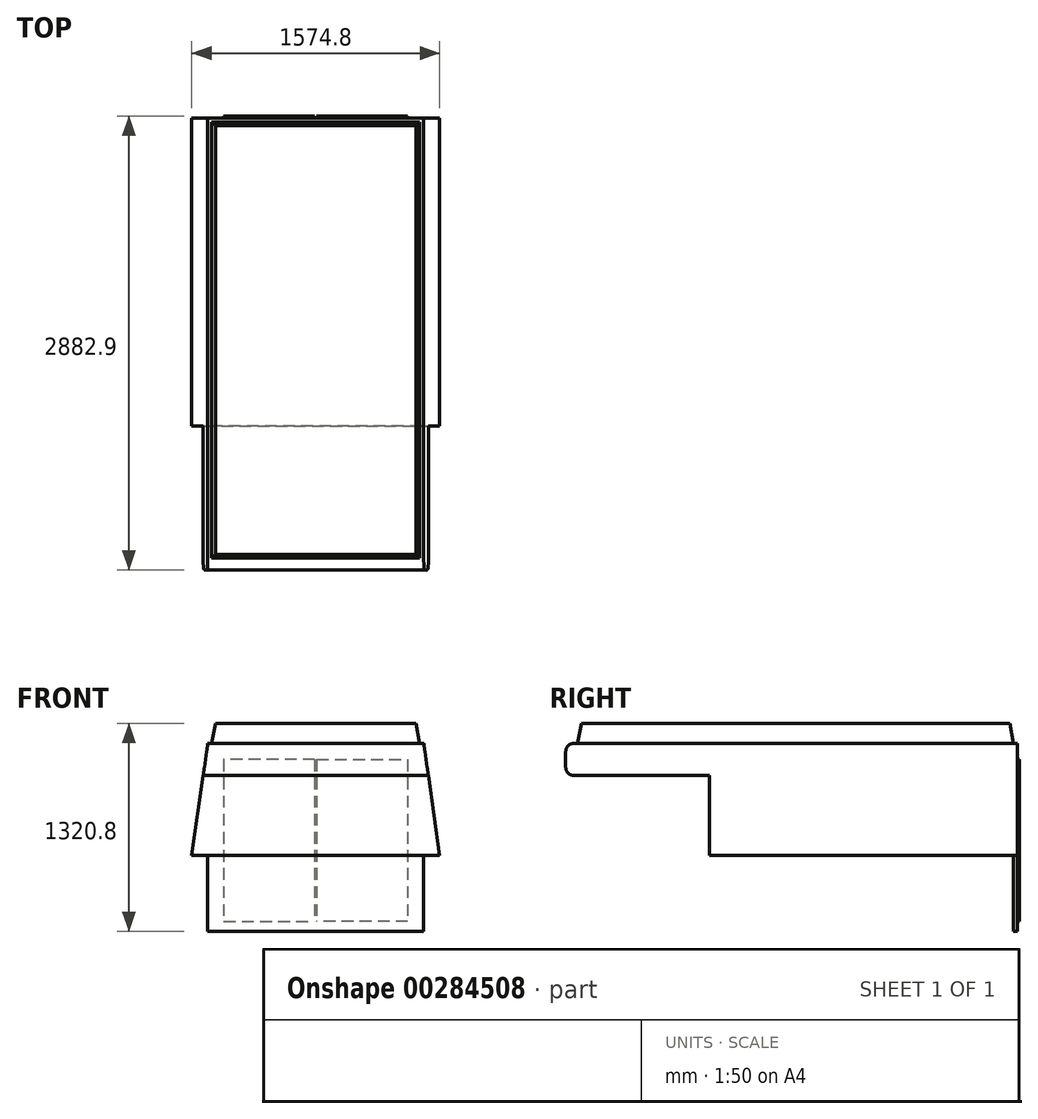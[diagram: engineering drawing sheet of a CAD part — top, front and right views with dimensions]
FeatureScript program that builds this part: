
annotation { "Feature Type Name" : "Feature", "Feature Type Description" : "" }
export const myFeature = defineFeature(function(context is Context, id is Id, definition is map)
    precondition{}
    {
        {
            var Q0;
            Q0=qCreatedBy(makeId("Front.planeOp"),FACE);
            var sketch = newSketch(context, id + "F0", { "sketchPlane" : qUnion([Q0])});
            skLineSegment(sketch, "E0", {"start": v(0, 0) * mm, "end": v(787.4, 0) * mm});
            skLineSegment(sketch, "E1", {"start": v(787.4, 0) * mm, "end": v(685.8, 711.2) * mm});
            skLineSegment(sketch, "E2", {"start": v(685.8, 711.2) * mm, "end": v(0, 711.2) * mm});
            skLineSegment(sketch, "E3", {"start": v(0, 711.2) * mm, "end": v(0, 0) * mm, "construction": true});
            skLineSegment(sketch, "E4.MirrorCS", {"start": v(-685.8, 711.2) * mm, "end": v(0, 711.2) * mm});
            skLineSegment(sketch, "E5.MirrorCS", {"start": v(-787.4, 0) * mm, "end": v(-685.8, 711.2) * mm});
            skLineSegment(sketch, "E6.MirrorCS", {"start": v(0, 0) * mm, "end": v(-787.4, 0) * mm});
            skSolve(sketch);
        }
        {
            var Q0;
            Q0=makeQuery(id+"F0.imprint","IMPRINT",FACE,{"disambiguationData":[TD([[makeQuery(id+"F0.imprint","IMPRINT",EDGE,{"derivedFrom":sQuery(id+"F0.wireOp",EDGE,"E0")}),1.0]])]});
            extrude(context, id + "F1", {"entities" : qUnion([Q0]), "depth" : 1955.8 * mm, "offsetDistance" : 25.4 * mm});
        }
        {
            var Q0;
            Q0=makeQuery(id+"F1.opExtrude","CAP_FACE",FACE,{"disambiguationData":[OSD([sQuery(id+"F0.wireOp",EDGE,"E0"),sQuery(id+"F0.wireOp",EDGE,"E1"),sQuery(id+"F0.wireOp",EDGE,"E2"),sQuery(id+"F0.wireOp",EDGE,"E4.MirrorCS"),sQuery(id+"F0.wireOp",EDGE,"E5.MirrorCS"),sQuery(id+"F0.wireOp",EDGE,"E6.MirrorCS")])],"isStart":false});
            var sketch = newSketch(context, id + "F2", { "sketchPlane" : qUnion([Q0])});
            skLineSegment(sketch, "E7", {"start": v(-714.83, 508) * mm, "end": v(714.83, 508) * mm});
            skSolve(sketch);
        }
        {
            var Q0;
            {var subQ0=sQuery(id+"F2.wireOp",EDGE,"E7");Q0=makeQuery(id+"F2.imprint","IMPRINT",FACE,{"disambiguationData":[TD([[makeQuery(id+"F2.imprint","IMPRINT",EDGE,{"derivedFrom":subQ0}),1.0]])]});}
            extrude(context, id + "F3", {"entities" : qUnion([Q0]), "operationType" : NewBodyOperationType.ADD, "depth" : 914.4 * mm, "offsetDistance" : 25.4 * mm});
        }
        {
            var Q0;
            Q0=makeQuery(id+"F3.opExtrude","CAP_EDGE",EDGE,{"disambiguationData":[OSD([sQuery(id+"F0.wireOp",EDGE,"E2"),sQuery(id+"F0.wireOp",EDGE,"E4.MirrorCS")])],"isStart":false});
            var Q1;
            Q1=makeQuery(id+"F3.opExtrude","CAP_EDGE",EDGE,{"disambiguationData":[OSD([sQuery(id+"F2.wireOp",EDGE,"E7")])],"isStart":false});
            fillet(context, id + "F4", {"entities" : qUnion([Q0, Q1]), "radius" : 50.8 * mm, "tangentPropagation" : true, "allowEdgeOverflow" : false});
        }
        {
            var Q0;
            {var subQ0=sQuery(id+"F0.wireOp",EDGE,"E4.MirrorCS");var subQ1=sQuery(id+"F0.wireOp",EDGE,"E2");Q0=makeQuery(id+"F3.boolean.opBoolean","MERGE",FACE,{"derivedFrom":[makeQuery(id+"F1.opExtrude","SWEPT_FACE",FACE,{"disambiguationData":[OSD([subQ1,subQ0])]}),makeQuery(id+"F3.opExtrude","SWEPT_FACE",FACE,{"disambiguationData":[OSD([subQ1,subQ0])]})]});}
            var sketch = newSketch(context, id + "F5", { "sketchPlane" : qUnion([Q0])});
            skLineSegment(sketch, "E8.0", {"start": v(-660.4, -25.4) * mm, "end": v(-660.4, -2794) * mm});
            skLineSegment(sketch, "E8.1", {"start": v(660.4, -25.4) * mm, "end": v(-660.4, -25.4) * mm});
            skLineSegment(sketch, "E8.2", {"start": v(660.4, -2794) * mm, "end": v(660.4, -25.4) * mm});
            skLineSegment(sketch, "E8.3", {"start": v(-660.4, -2794) * mm, "end": v(660.4, -2794) * mm});
            skSolve(sketch);
        }
        {
            var Q0;
            Q0=makeQuery(id+"F5.imprint","IMPRINT",FACE,{"disambiguationData":[TD([[makeQuery(id+"F5.imprint","IMPRINT",EDGE,{"derivedFrom":sQuery(id+"F5.wireOp",EDGE,"E8.0")}),1.0]])]});
            extrude(context, id + "F6", {"entities" : qUnion([Q0]), "depth" : 127 * mm, "hasDraft" : true, "draftAngle" : 10 * degree, "draftPullDirection" : true});
        }
        {
            var Q0;
            Q0=makeQuery(id+"F1.opExtrude","CAP_FACE",FACE,{"disambiguationData":[OSD([sQuery(id+"F0.wireOp",EDGE,"E0"),sQuery(id+"F0.wireOp",EDGE,"E1"),sQuery(id+"F0.wireOp",EDGE,"E2"),sQuery(id+"F0.wireOp",EDGE,"E4.MirrorCS"),sQuery(id+"F0.wireOp",EDGE,"E5.MirrorCS"),sQuery(id+"F0.wireOp",EDGE,"E6.MirrorCS")])],"isStart":true});
            var sketch = newSketch(context, id + "F7", { "sketchPlane" : qUnion([Q0])});
            skLineSegment(sketch, "E9.bottom", {"start": v(685.8, 0) * mm, "end": v(-685.8, 0) * mm});
            skLineSegment(sketch, "E9.top", {"start": v(685.8, -482.6) * mm, "end": v(-685.8, -482.6) * mm});
            skLineSegment(sketch, "E9.left", {"start": v(685.8, 0) * mm, "end": v(685.8, -482.6) * mm});
            skLineSegment(sketch, "E9.right", {"start": v(-685.8, 0) * mm, "end": v(-685.8, -482.6) * mm});
            skPoint(sketch, "E9.middle", {"position": v(0, -241.3) * mm});
            skSolve(sketch);
        }
        {
            var Q0;
            Q0=makeQuery(id+"F7.imprint","IMPRINT",FACE,{"disambiguationData":[TD([[makeQuery(id+"F7.imprint","IMPRINT",EDGE,{"derivedFrom":sQuery(id+"F7.wireOp",EDGE,"E9.bottom")}),-1.0]])]});
            extrude(context, id + "F8", {"entities" : qUnion([Q0]), "operationType" : NewBodyOperationType.ADD, "oppositeDirection" : true, "depth" : 25.4 * mm});
        }
        {
            var Q0;
            Q0=makeQuery(id+"F8.boolean.opBoolean","MERGE",FACE,{"derivedFrom":[makeQuery(id+"F1.opExtrude","CAP_FACE",FACE,{"disambiguationData":[OSD([sQuery(id+"F0.wireOp",EDGE,"E0"),sQuery(id+"F0.wireOp",EDGE,"E1"),sQuery(id+"F0.wireOp",EDGE,"E2"),sQuery(id+"F0.wireOp",EDGE,"E4.MirrorCS"),sQuery(id+"F0.wireOp",EDGE,"E5.MirrorCS"),sQuery(id+"F0.wireOp",EDGE,"E6.MirrorCS")])],"isStart":true}),makeQuery(id+"F8.opExtrude","CAP_FACE",FACE,{"disambiguationData":[OSD([sQuery(id+"F7.wireOp",EDGE,"E9.bottom"),sQuery(id+"F7.wireOp",EDGE,"E9.top"),sQuery(id+"F7.wireOp",EDGE,"E9.left"),sQuery(id+"F7.wireOp",EDGE,"E9.right")])],"isStart":true})]});
            var sketch = newSketch(context, id + "F9", { "sketchPlane" : qUnion([Q0])});
            skLineSegment(sketch, "E10", {"start": v(0, -419.1) * mm, "end": v(0, 609.6) * mm});
            skLineSegment(sketch, "E11", {"start": v(0, 609.6) * mm, "end": v(584.2, 609.6) * mm});
            skLineSegment(sketch, "E12", {"start": v(584.2, 609.6) * mm, "end": v(584.2, -419.1) * mm});
            skLineSegment(sketch, "E13", {"start": v(584.2, -419.1) * mm, "end": v(0, -419.1) * mm});
            skLineSegment(sketch, "E14.MirrorCS", {"start": v(0, 609.6) * mm, "end": v(-584.2, 609.6) * mm});
            skLineSegment(sketch, "E15.MirrorCS", {"start": v(-584.2, 609.6) * mm, "end": v(-584.2, -419.1) * mm});
            skLineSegment(sketch, "E16.MirrorCS", {"start": v(-584.2, -419.1) * mm, "end": v(0, -419.1) * mm});
            skLineSegment(sketch, "E17", {"start": v(6.35, 609.6) * mm, "end": v(6.35, -419.1) * mm});
            skLineSegment(sketch, "E18.MirrorCS", {"start": v(-6.35, 609.6) * mm, "end": v(-6.35, -419.1) * mm});
            skSolve(sketch);
        }
        {
            var Q0;
            {var subQ0=sQuery(id+"F9.wireOp",EDGE,"E15.MirrorCS");Q0=makeQuery(id+"F9.imprint","IMPRINT",FACE,{"disambiguationData":[TD([[makeQuery(id+"F9.imprint","IMPRINT",EDGE,{"derivedFrom":subQ0}),1.0]])]});}
            var Q1;
            {var subQ0=sQuery(id+"F9.wireOp",EDGE,"E12");Q1=makeQuery(id+"F9.imprint","IMPRINT",FACE,{"disambiguationData":[TD([[makeQuery(id+"F9.imprint","IMPRINT",EDGE,{"derivedFrom":subQ0}),-1.0]])]});}
            extrude(context, id + "F10", {"entities" : qUnion([Q0, Q1]), "depth" : 12.7 * mm});
        }
    });
